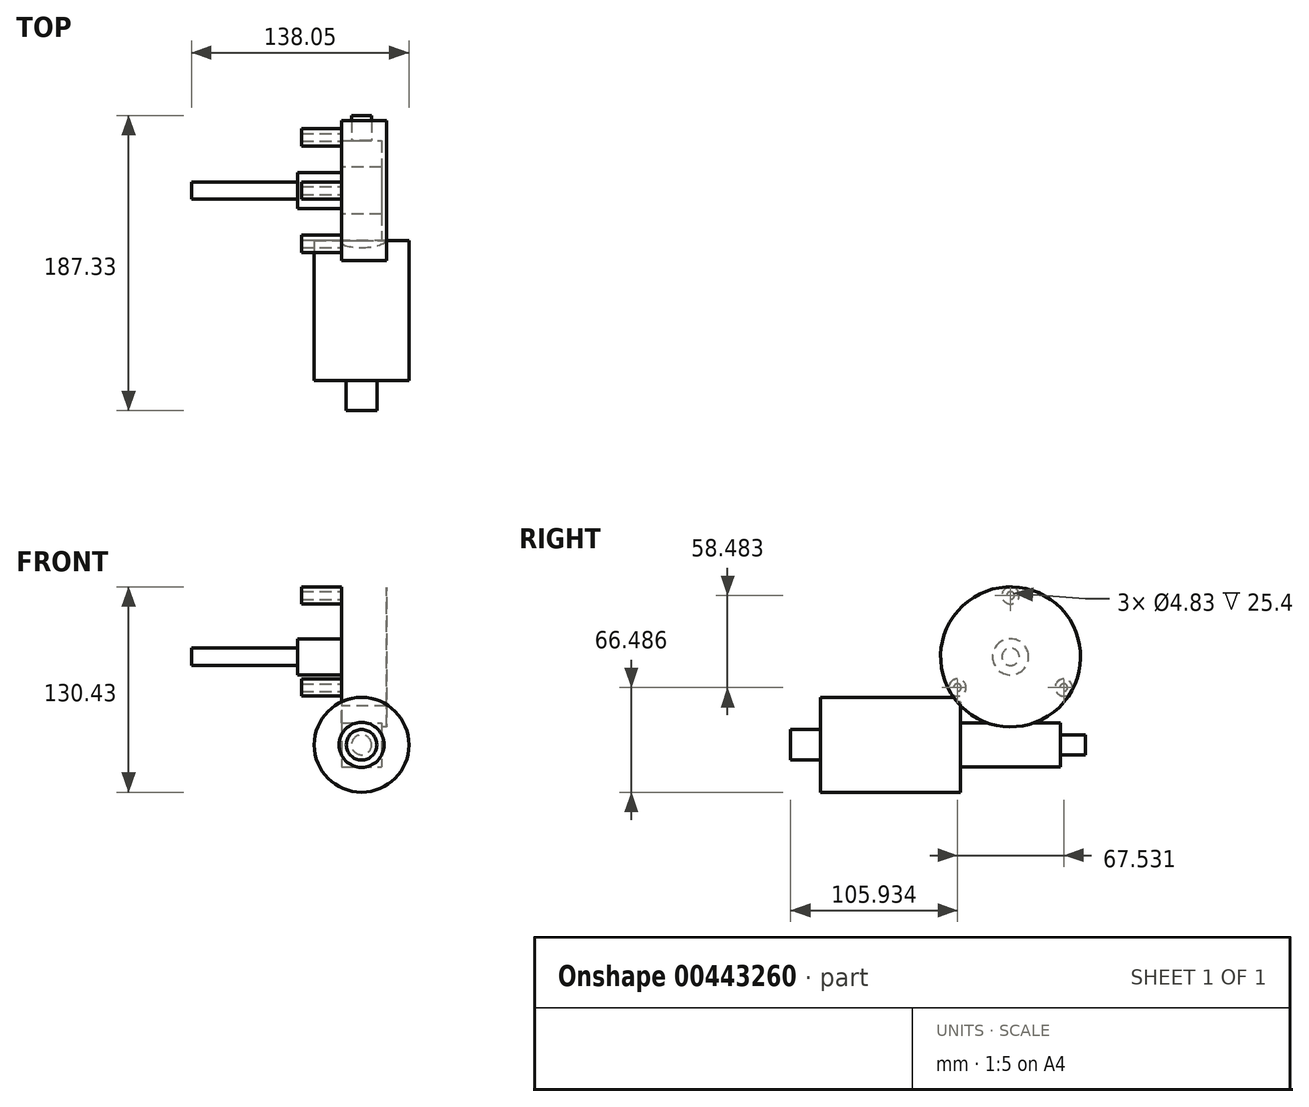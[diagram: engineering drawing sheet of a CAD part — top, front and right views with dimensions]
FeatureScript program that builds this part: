
annotation { "Feature Type Name" : "Feature", "Feature Type Description" : "" }
export const myFeature = defineFeature(function(context is Context, id is Id, definition is map)
    precondition{}
    {
        {
            var Q0;
            Q0=qCreatedBy(makeId("Front.planeOp"),FACE);
            var sketch = newSketch(context, id + "F0", { "sketchPlane" : qUnion([Q0])});
            skCircle(sketch, "E0", {"center": v(0, 0) * mm, "radius": 30.1 * mm});
            skCircle(sketch, "E1", {"center": v(0, 0) * mm, "radius": 14.29 * mm});
            skCircle(sketch, "E2", {"center": v(0, 0) * mm, "radius": 9.72 * mm});
            skSolve(sketch);
        }
        {
            var Q0;
            Q0 = qSketchRegion(id + "F0", true);
            var Q1;
            Q1=makeQuery(id+"F0.imprint","IMPRINT",FACE,{"disambiguationData":[TD([[makeQuery(id+"F0.imprint","IMPRINT",EDGE,{"derivedFrom":sQuery(id+"F0.wireOp",EDGE,"E1")}),1.0]])]});
            var Q2;
            Q2=makeQuery(id+"F0.imprint","IMPRINT",FACE,{"disambiguationData":[TD([[makeQuery(id+"F0.imprint","IMPRINT",EDGE,{"derivedFrom":sQuery(id+"F0.wireOp",EDGE,"E2")}),1.0]])]});
            extrude(context, id + "F1", {"entities" : qUnion([Q0, Q1, Q2]), "oppositeDirection" : true, "depth" : 88.9 * mm});
        }
        {
            var Q0;
            Q0=makeQuery(id+"F0.imprint","IMPRINT",FACE,{"disambiguationData":[TD([[makeQuery(id+"F0.imprint","IMPRINT",EDGE,{"derivedFrom":sQuery(id+"F0.wireOp",EDGE,"E1")}),1.0]])]});
            extrude(context, id + "F2", {"entities" : qUnion([Q0]), "operationType" : NewBodyOperationType.ADD, "depth" : 5 / 406.4 * mm});
        }
        {
            var Q0;
            Q0=makeQuery(id+"F0.imprint","IMPRINT",FACE,{"disambiguationData":[TD([[makeQuery(id+"F0.imprint","IMPRINT",EDGE,{"derivedFrom":sQuery(id+"F0.wireOp",EDGE,"E2")}),1.0]])]});
            extrude(context, id + "F3", {"entities" : qUnion([Q0]), "operationType" : NewBodyOperationType.ADD, "depth" : 19.05 * mm});
        }
        {
            var Q0;
            Q0=makeQuery(id+"F1.opExtrude","CAP_FACE",FACE,{"disambiguationData":[OSD([sQuery(id+"F0.wireOp",EDGE,"E0")])],"isStart":false});
            var sketch = newSketch(context, id + "F4", { "sketchPlane" : qUnion([Q0])});
            skLineSegment(sketch, "E3.bottom", {"start": v(12.7, 13.97) * mm, "end": v(-12.7, 13.97) * mm});
            skLineSegment(sketch, "E3.top", {"start": v(12.7, -13.97) * mm, "end": v(-12.7, -13.97) * mm});
            skLineSegment(sketch, "E3.left", {"start": v(12.7, 13.97) * mm, "end": v(12.7, -13.97) * mm});
            skLineSegment(sketch, "E3.right", {"start": v(-12.7, 13.97) * mm, "end": v(-12.7, -13.97) * mm});
            skPoint(sketch, "E3.middle", {"position": v(0, 0) * mm});
            skCircle(sketch, "E4", {"center": v(0, 0) * mm, "radius": 6.35 * mm});
            skSolve(sketch);
        }
        {
            var Q0;
            Q0 = qSketchRegion(id + "F4", true);
            extrude(context, id + "F5", {"entities" : qUnion([Q0]), "operationType" : NewBodyOperationType.ADD, "depth" : 63.5 * mm});
        }
        {
            var Q0;
            Q0=makeQuery(id+"F4.imprint","IMPRINT",FACE,{"disambiguationData":[TD([[makeQuery(id+"F4.imprint","IMPRINT",EDGE,{"derivedFrom":sQuery(id+"F4.wireOp",EDGE,"E4")}),1.0]])]});
            extrude(context, id + "F6", {"entities" : qUnion([Q0]), "operationType" : NewBodyOperationType.ADD, "depth" : 79.38 * mm});
        }
        {
            var Q0;
            Q0=makeQuery(id+"F5.opExtrude","SWEPT_FACE",FACE,{"disambiguationData":[OSD([sQuery(id+"F4.wireOp",EDGE,"E3.left")])]});
            var sketch = newSketch(context, id + "F7", { "sketchPlane" : qUnion([Q0])});
            skLineSegment(sketch, "E5", {"start": v(-120.65, 13.97) * mm, "end": v(-120.65, 11.43) * mm});
            skLineSegment(sketch, "E6", {"start": v(-120.65, 11.43) * mm, "end": v(-120.65, 55.88) * mm});
            skCircle(sketch, "E7", {"center": v(-120.65, 55.88) * mm, "radius": 44.45 * mm});
            skCircle(sketch, "E8", {"center": v(-120.65, 55.88) * mm, "radius": 5.52 * mm});
            skCircle(sketch, "E9", {"center": v(-120.65, 55.88) * mm, "radius": 11.43 * mm});
            skCircle(sketch, "E10.cCircle", {"center": v(-120.65, 55.88) * mm, "radius": 44.45 * mm, "construction": true});
            skLineSegment(sketch, "E11.0", {"start": v(-120.65, 100.33) * mm, "end": v(-82.16, 33.66) * mm});
            skLineSegment(sketch, "E11.1", {"start": v(-82.16, 33.66) * mm, "end": v(-159.14, 33.65) * mm});
            skLineSegment(sketch, "E11.2", {"start": v(-159.14, 33.65) * mm, "end": v(-120.65, 100.33) * mm});
            skLineSegment(sketch, "E12", {"start": v(-120.65, 55.88) * mm, "end": v(-82.16, 33.66) * mm});
            skLineSegment(sketch, "E13", {"start": v(-120.65, 55.88) * mm, "end": v(-120.65, 100.33) * mm});
            skLineSegment(sketch, "E14", {"start": v(-120.65, 55.88) * mm, "end": v(-159.14, 33.65) * mm});
            skLineSegment(sketch, "E15", {"start": v(-159.14, 33.65) * mm, "end": v(-154.42, 36.39) * mm});
            skCircle(sketch, "E16", {"center": v(-154.42, 36.39) * mm, "radius": 5.46 * mm});
            skLineSegment(sketch, "E17", {"start": v(-82.16, 33.66) * mm, "end": v(-86.88, 36.39) * mm});
            skLineSegment(sketch, "E18", {"start": v(-120.65, 100.33) * mm, "end": v(-120.65, 94.87) * mm});
            skCircle(sketch, "E19", {"center": v(-120.65, 94.87) * mm, "radius": 5.46 * mm});
            skCircle(sketch, "E20", {"center": v(-86.88, 36.39) * mm, "radius": 5.46 * mm});
            skCircle(sketch, "E21", {"center": v(-154.42, 36.39) * mm, "radius": 2.41 * mm});
            skCircle(sketch, "E22", {"center": v(-86.88, 36.39) * mm, "radius": 2.41 * mm});
            skCircle(sketch, "E23", {"center": v(-120.65, 94.87) * mm, "radius": 2.41 * mm});
            skSolve(sketch);
        }
        {
            var Q0;
            Q0 = qSketchRegion(id + "F7", true);
            var Q1;
            Q1=makeQuery(id+"F7.imprint","IMPRINT",FACE,{"disambiguationData":[TD([[makeQuery(id+"F7.imprint","IMPRINT",EDGE,{"derivedFrom":sQuery(id+"F7.wireOp",EDGE,"E8")}),-1.0]])]});
            var Q2;
            Q2=makeQuery(id+"F7.imprint","IMPRINT",FACE,{"disambiguationData":[TD([[makeQuery(id+"F7.imprint","IMPRINT",EDGE,{"derivedFrom":sQuery(id+"F7.wireOp",EDGE,"E8")}),1.0]])]});
            var Q3;
            {var subQ1=sQuery(id+"F7.wireOp",EDGE,"E9");var subQ9=sQuery(id+"F7.wireOp",EDGE,"E13");var subQ10=makeQuery(id+"F7.imprint","INTERSECT",VERTEX,{"derivedFrom":[subQ1,subQ9]});Q3=makeQuery(id+"F7.imprint","IMPRINT",FACE,{"disambiguationData":[TD([[makeQuery(id+"F7.imprint","IMPRINT",EDGE,{"disambiguationData":[TD([[subQ10,1.0]])],"derivedFrom":subQ1}),-1.0]])]});}
            var Q4;
            {var subQ0=sQuery(id+"F7.wireOp",EDGE,"E14");var subQ1=sQuery(id+"F7.wireOp",EDGE,"E9");var subQ2=makeQuery(id+"F7.imprint","INTERSECT",VERTEX,{"derivedFrom":[subQ1,subQ0]});Q4=makeQuery(id+"F7.imprint","IMPRINT",FACE,{"disambiguationData":[TD([[makeQuery(id+"F7.imprint","IMPRINT",EDGE,{"disambiguationData":[TD([[subQ2,1.0]])],"derivedFrom":subQ1}),-1.0]])]});}
            var Q5;
            {var subQ5=sQuery(id+"F7.wireOp",EDGE,"E11.1");var subQ6=sQuery(id+"F7.wireOp",EDGE,"E6");var subQ7=makeQuery(id+"F7.imprint","INTERSECT",VERTEX,{"derivedFrom":[subQ6,subQ5]});Q5=makeQuery(id+"F7.imprint","IMPRINT",FACE,{"disambiguationData":[TD([[makeQuery(id+"F7.imprint","IMPRINT",EDGE,{"disambiguationData":[TD([[subQ7,-1.0]])],"derivedFrom":subQ6}),1.0]])]});}
            var Q6;
            {var subQ5=sQuery(id+"F7.wireOp",EDGE,"E11.1");var subQ7=sQuery(id+"F7.wireOp",EDGE,"E6");var subQ8=makeQuery(id+"F7.imprint","INTERSECT",VERTEX,{"derivedFrom":[subQ7,subQ5]});Q6=makeQuery(id+"F7.imprint","IMPRINT",FACE,{"disambiguationData":[TD([[makeQuery(id+"F7.imprint","IMPRINT",EDGE,{"disambiguationData":[TD([[subQ8,-1.0]])],"derivedFrom":subQ7}),-1.0]])]});}
            var Q7;
            {var subQ0=sQuery(id+"F7.wireOp",EDGE,"E15");var subQ1=sQuery(id+"F7.wireOp",EDGE,"E14");var subQ2=makeQuery(id+"F7.imprint","INTERSECT",VERTEX,{"derivedFrom":[subQ1,subQ0]});Q7=makeQuery(id+"F7.imprint","IMPRINT",FACE,{"disambiguationData":[TD([[makeQuery(id+"F7.imprint","IMPRINT",EDGE,{"disambiguationData":[TD([[subQ2,1.0]])],"derivedFrom":subQ1}),-1.0]])]});}
            var Q8;
            {var subQ0=sQuery(id+"F7.wireOp",EDGE,"E15");var subQ1=sQuery(id+"F7.wireOp",EDGE,"E14");var subQ2=makeQuery(id+"F7.imprint","INTERSECT",VERTEX,{"derivedFrom":[subQ1,subQ0]});Q8=makeQuery(id+"F7.imprint","IMPRINT",FACE,{"disambiguationData":[TD([[makeQuery(id+"F7.imprint","IMPRINT",EDGE,{"disambiguationData":[TD([[subQ2,1.0]])],"derivedFrom":subQ1}),1.0]])]});}
            var Q9;
            {var subQ0=sQuery(id+"F7.wireOp",EDGE,"E17");var subQ1=sQuery(id+"F7.wireOp",EDGE,"E12");var subQ2=makeQuery(id+"F7.imprint","INTERSECT",VERTEX,{"derivedFrom":[subQ1,subQ0]});Q9=makeQuery(id+"F7.imprint","IMPRINT",FACE,{"disambiguationData":[TD([[makeQuery(id+"F7.imprint","IMPRINT",EDGE,{"disambiguationData":[TD([[subQ2,1.0]])],"derivedFrom":subQ1}),1.0]])]});}
            var Q10;
            {var subQ0=sQuery(id+"F7.wireOp",EDGE,"E17");var subQ1=sQuery(id+"F7.wireOp",EDGE,"E12");var subQ2=makeQuery(id+"F7.imprint","INTERSECT",VERTEX,{"derivedFrom":[subQ1,subQ0]});Q10=makeQuery(id+"F7.imprint","IMPRINT",FACE,{"disambiguationData":[TD([[makeQuery(id+"F7.imprint","IMPRINT",EDGE,{"disambiguationData":[TD([[subQ2,1.0]])],"derivedFrom":subQ1}),-1.0]])]});}
            var Q11;
            {var subQ0=sQuery(id+"F7.wireOp",EDGE,"E18");var subQ1=sQuery(id+"F7.wireOp",EDGE,"E13");var subQ2=makeQuery(id+"F7.imprint","INTERSECT",VERTEX,{"derivedFrom":[subQ1,subQ0]});Q11=makeQuery(id+"F7.imprint","IMPRINT",FACE,{"disambiguationData":[TD([[makeQuery(id+"F7.imprint","IMPRINT",EDGE,{"disambiguationData":[TD([[subQ2,1.0]])],"derivedFrom":subQ1}),1.0]])]});}
            var Q12;
            {var subQ0=sQuery(id+"F7.wireOp",EDGE,"E18");var subQ1=sQuery(id+"F7.wireOp",EDGE,"E13");var subQ2=makeQuery(id+"F7.imprint","INTERSECT",VERTEX,{"derivedFrom":[subQ1,subQ0]});Q12=makeQuery(id+"F7.imprint","IMPRINT",FACE,{"disambiguationData":[TD([[makeQuery(id+"F7.imprint","IMPRINT",EDGE,{"disambiguationData":[TD([[subQ2,1.0]])],"derivedFrom":subQ1}),-1.0]])]});}
            extrude(context, id + "F8", {"entities" : qUnion([Q0, Q1, Q2, Q3, Q4, Q5, Q6, Q7, Q8, Q9, Q10, Q11, Q12]), "operationType" : NewBodyOperationType.ADD, "oppositeDirection" : true, "depth" : 28.45 * mm});
        }
        {
            var Q0;
            Q0=makeQuery(id+"F7.imprint","IMPRINT",FACE,{"disambiguationData":[TD([[makeQuery(id+"F7.imprint","IMPRINT",EDGE,{"derivedFrom":sQuery(id+"F7.wireOp",EDGE,"E8")}),-1.0]])]});
            var Q1;
            Q1=makeQuery(id+"F7.imprint","IMPRINT",FACE,{"disambiguationData":[TD([[makeQuery(id+"F7.imprint","IMPRINT",EDGE,{"derivedFrom":sQuery(id+"F7.wireOp",EDGE,"E8")}),1.0]])]});
            extrude(context, id + "F9", {"entities" : qUnion([Q0, Q1]), "operationType" : NewBodyOperationType.ADD, "depth" : 27.94 * mm});
        }
        {
            var Q0;
            Q0=makeQuery(id+"F7.imprint","IMPRINT",FACE,{"disambiguationData":[TD([[makeQuery(id+"F7.imprint","IMPRINT",EDGE,{"derivedFrom":sQuery(id+"F7.wireOp",EDGE,"E8")}),1.0]])]});
            extrude(context, id + "F10", {"entities" : qUnion([Q0]), "operationType" : NewBodyOperationType.ADD, "depth" : 95.25 * mm});
        }
        {
            var Q0;
            {var subQ0=sQuery(id+"F7.wireOp",EDGE,"E16");var subQ1=sQuery(id+"F7.wireOp",EDGE,"E11.2");var subQ3=makeQuery(id+"F7.imprint","INTERSECT",VERTEX,{"derivedFrom":[subQ1,subQ0]});Q0=makeQuery(id+"F7.imprint","IMPRINT",FACE,{"disambiguationData":[TD([[makeQuery(id+"F7.imprint","IMPRINT",EDGE,{"disambiguationData":[TD([[subQ3,1.0]])],"derivedFrom":subQ1}),1.0]])]});}
            var Q1;
            {var subQ0=sQuery(id+"F7.wireOp",EDGE,"E16");var subQ1=sQuery(id+"F7.wireOp",EDGE,"E11.1");var subQ3=makeQuery(id+"F7.imprint","INTERSECT",VERTEX,{"derivedFrom":[subQ1,subQ0]});Q1=makeQuery(id+"F7.imprint","IMPRINT",FACE,{"disambiguationData":[TD([[makeQuery(id+"F7.imprint","IMPRINT",EDGE,{"disambiguationData":[TD([[subQ3,-1.0]])],"derivedFrom":subQ1}),1.0]])]});}
            var Q2;
            {var subQ0=sQuery(id+"F7.wireOp",EDGE,"E20");var subQ1=sQuery(id+"F7.wireOp",EDGE,"E11.1");var subQ3=makeQuery(id+"F7.imprint","INTERSECT",VERTEX,{"derivedFrom":[subQ1,subQ0]});Q2=makeQuery(id+"F7.imprint","IMPRINT",FACE,{"disambiguationData":[TD([[makeQuery(id+"F7.imprint","IMPRINT",EDGE,{"disambiguationData":[TD([[subQ3,1.0]])],"derivedFrom":subQ1}),1.0]])]});}
            var Q3;
            {var subQ0=sQuery(id+"F7.wireOp",EDGE,"E20");var subQ1=sQuery(id+"F7.wireOp",EDGE,"E11.0");var subQ3=makeQuery(id+"F7.imprint","INTERSECT",VERTEX,{"derivedFrom":[subQ1,subQ0]});Q3=makeQuery(id+"F7.imprint","IMPRINT",FACE,{"disambiguationData":[TD([[makeQuery(id+"F7.imprint","IMPRINT",EDGE,{"disambiguationData":[TD([[subQ3,-1.0]])],"derivedFrom":subQ1}),1.0]])]});}
            var Q4;
            {var subQ0=sQuery(id+"F7.wireOp",EDGE,"E19");var subQ1=sQuery(id+"F7.wireOp",EDGE,"E11.0");var subQ3=makeQuery(id+"F7.imprint","INTERSECT",VERTEX,{"derivedFrom":[subQ1,subQ0]});Q4=makeQuery(id+"F7.imprint","IMPRINT",FACE,{"disambiguationData":[TD([[makeQuery(id+"F7.imprint","IMPRINT",EDGE,{"disambiguationData":[TD([[subQ3,1.0]])],"derivedFrom":subQ1}),1.0]])]});}
            var Q5;
            {var subQ0=sQuery(id+"F7.wireOp",EDGE,"E19");var subQ1=sQuery(id+"F7.wireOp",EDGE,"E11.2");var subQ3=makeQuery(id+"F7.imprint","INTERSECT",VERTEX,{"derivedFrom":[subQ1,subQ0]});Q5=makeQuery(id+"F7.imprint","IMPRINT",FACE,{"disambiguationData":[TD([[makeQuery(id+"F7.imprint","IMPRINT",EDGE,{"disambiguationData":[TD([[subQ3,-1.0]])],"derivedFrom":subQ1}),1.0]])]});}
            var Q6;
            {var subQ0=sQuery(id+"F7.wireOp",EDGE,"E20");var subQ3=sQuery(id+"F7.wireOp",EDGE,"E12");var subQ4=makeQuery(id+"F7.imprint","INTERSECT",VERTEX,{"derivedFrom":[subQ3,subQ0]});Q6=makeQuery(id+"F7.imprint","IMPRINT",FACE,{"disambiguationData":[TD([[makeQuery(id+"F7.imprint","IMPRINT",EDGE,{"disambiguationData":[TD([[subQ4,-1.0]])],"derivedFrom":subQ3}),1.0]])]});}
            var Q7;
            {var subQ0=sQuery(id+"F7.wireOp",EDGE,"E20");var subQ3=sQuery(id+"F7.wireOp",EDGE,"E12");var subQ4=makeQuery(id+"F7.imprint","INTERSECT",VERTEX,{"derivedFrom":[subQ3,subQ0]});Q7=makeQuery(id+"F7.imprint","IMPRINT",FACE,{"disambiguationData":[TD([[makeQuery(id+"F7.imprint","IMPRINT",EDGE,{"disambiguationData":[TD([[subQ4,-1.0]])],"derivedFrom":subQ3}),-1.0]])]});}
            var Q8;
            {var subQ0=sQuery(id+"F7.wireOp",EDGE,"E16");var subQ3=sQuery(id+"F7.wireOp",EDGE,"E14");var subQ4=makeQuery(id+"F7.imprint","INTERSECT",VERTEX,{"derivedFrom":[subQ3,subQ0]});Q8=makeQuery(id+"F7.imprint","IMPRINT",FACE,{"disambiguationData":[TD([[makeQuery(id+"F7.imprint","IMPRINT",EDGE,{"disambiguationData":[TD([[subQ4,-1.0]])],"derivedFrom":subQ3}),1.0]])]});}
            var Q9;
            {var subQ0=sQuery(id+"F7.wireOp",EDGE,"E16");var subQ6=sQuery(id+"F7.wireOp",EDGE,"E14");var subQ7=makeQuery(id+"F7.imprint","INTERSECT",VERTEX,{"derivedFrom":[subQ6,subQ0]});Q9=makeQuery(id+"F7.imprint","IMPRINT",FACE,{"disambiguationData":[TD([[makeQuery(id+"F7.imprint","IMPRINT",EDGE,{"disambiguationData":[TD([[subQ7,-1.0]])],"derivedFrom":subQ6}),-1.0]])]});}
            var Q10;
            {var subQ0=sQuery(id+"F7.wireOp",EDGE,"E19");var subQ3=sQuery(id+"F7.wireOp",EDGE,"E13");var subQ4=makeQuery(id+"F7.imprint","INTERSECT",VERTEX,{"derivedFrom":[subQ3,subQ0]});Q10=makeQuery(id+"F7.imprint","IMPRINT",FACE,{"disambiguationData":[TD([[makeQuery(id+"F7.imprint","IMPRINT",EDGE,{"disambiguationData":[TD([[subQ4,-1.0]])],"derivedFrom":subQ3}),-1.0]])]});}
            var Q11;
            {var subQ0=sQuery(id+"F7.wireOp",EDGE,"E19");var subQ3=sQuery(id+"F7.wireOp",EDGE,"E13");var subQ4=makeQuery(id+"F7.imprint","INTERSECT",VERTEX,{"derivedFrom":[subQ3,subQ0]});Q11=makeQuery(id+"F7.imprint","IMPRINT",FACE,{"disambiguationData":[TD([[makeQuery(id+"F7.imprint","IMPRINT",EDGE,{"disambiguationData":[TD([[subQ4,-1.0]])],"derivedFrom":subQ3}),1.0]])]});}
            extrude(context, id + "F11", {"entities" : qUnion([Q0, Q1, Q2, Q3, Q4, Q5, Q6, Q7, Q8, Q9, Q10, Q11]), "operationType" : NewBodyOperationType.ADD, "depth" : 25.4 * mm});
        }
    });
